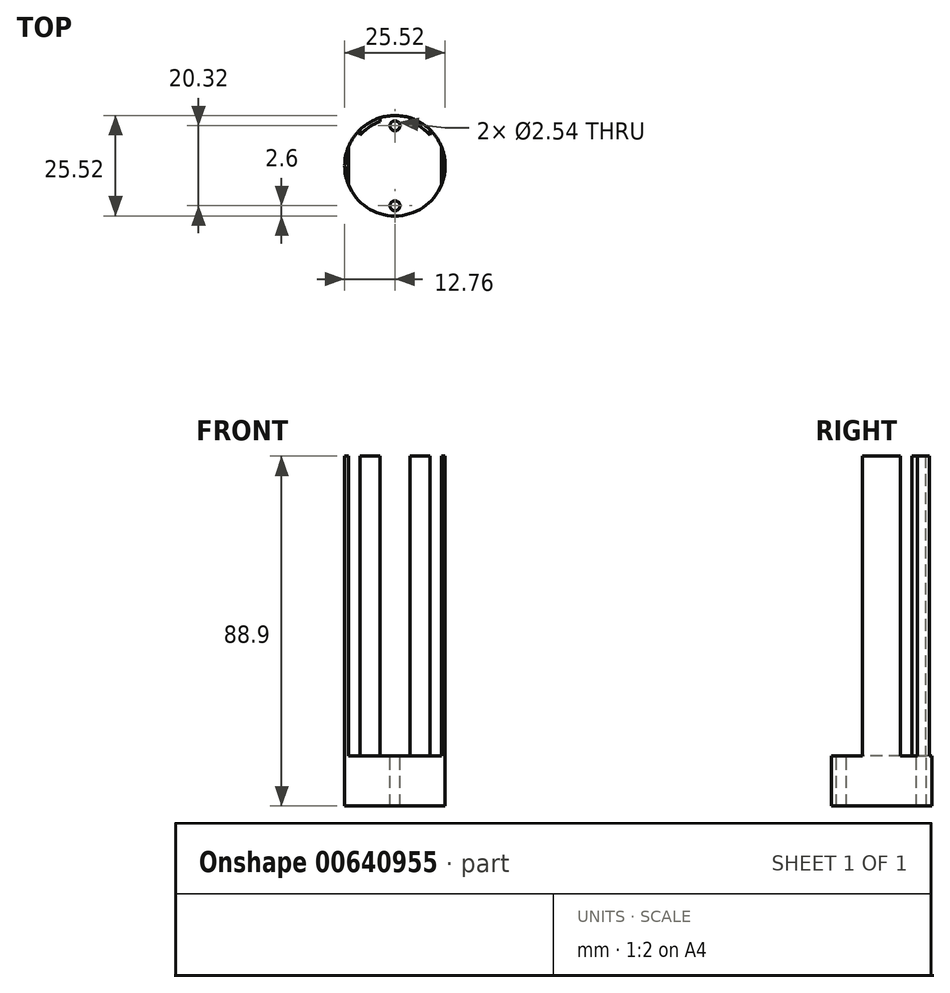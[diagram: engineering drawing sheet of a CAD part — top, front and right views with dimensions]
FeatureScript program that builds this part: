
annotation { "Feature Type Name" : "Feature", "Feature Type Description" : "" }
export const myFeature = defineFeature(function(context is Context, id is Id, definition is map)
    precondition{}
    {
        {
            var Q0;
            Q0=qCreatedBy(makeId("Top.planeOp"),FACE);
            var sketch = newSketch(context, id + "F0", { "sketchPlane" : qUnion([Q0])});
            skArc(sketch, "E0", {"start": v(-3.81, 12.18) * mm, "mid": v(-6.53, 10.97) * mm, "end": v(-8.9, 9.16) * mm});
            skArc(sketch, "E1", {"start": v(-3.81, 11.18) * mm, "mid": v(-6.57, 9.81) * mm, "end": v(-8.9, 7.78) * mm});
            skLineSegment(sketch, "E2", {"start": v(-11.81, 4.84) * mm, "end": v(-11.81, -4.84) * mm});
            skLineSegment(sketch, "E3", {"start": v(11.81, 4.84) * mm, "end": v(11.81, -4.84) * mm});
            skLineSegment(sketch, "E4", {"start": v(-3.81, 12.18) * mm, "end": v(-3.81, 11.18) * mm});
            skLineSegment(sketch, "E5", {"start": v(3.81, 12.18) * mm, "end": v(3.81, 11.18) * mm});
            skLineSegment(sketch, "E6", {"start": v(-8.9, 9.16) * mm, "end": v(-8.9, 7.78) * mm});
            skLineSegment(sketch, "E7", {"start": v(8.9, 9.16) * mm, "end": v(8.9, 7.78) * mm});
            skArc(sketch, "E8.trimOffspring", {"start": v(-11.81, 4.84) * mm, "mid": v(-12.76, 0) * mm, "end": v(-11.81, -4.84) * mm});
            skArc(sketch, "E9.trimOffspring", {"start": v(8.9, 9.16) * mm, "mid": v(6.53, 10.97) * mm, "end": v(3.81, 12.18) * mm});
            skArc(sketch, "E10.trimOffspring", {"start": v(8.9, 7.78) * mm, "mid": v(6.57, 9.81) * mm, "end": v(3.81, 11.18) * mm});
            skArc(sketch, "E11.trimOffspring", {"start": v(11.81, -4.84) * mm, "mid": v(12.76, 0) * mm, "end": v(11.81, 4.84) * mm});
            skSolve(sketch);
        }
        {
            var Q0;
            Q0=qCreatedBy(makeId("Top.planeOp"),FACE);
            var sketch = newSketch(context, id + "F1", { "sketchPlane" : qUnion([Q0])});
            skCircle(sketch, "E12", {"center": v(0, 0) * mm, "radius": 12.76 * mm});
            skPoint(sketch, "E13", {"position": v(0, 10.16) * mm});
            skPoint(sketch, "E14", {"position": v(0, -10.16) * mm});
            skCircle(sketch, "E15", {"center": v(0, 10.16) * mm, "radius": 1.27 * mm});
            skCircle(sketch, "E16", {"center": v(0, -10.16) * mm, "radius": 1.27 * mm});
            skSolve(sketch);
        }
        {
            var Q0;
            Q0 = qSketchRegion(id + "F1", true);
            extrude(context, id + "F2", {"entities" : qUnion([Q0]), "oppositeDirection" : true, "depth" : 12.7 * mm, "offsetDistance" : 25.4 * mm});
        }
        {
            var Q0;
            Q0 = qSketchRegion(id + "F0", true);
            extrude(context, id + "F3", {"entities" : qUnion([Q0]), "operationType" : NewBodyOperationType.ADD, "depth" : 76.2 * mm, "offsetDistance" : 25.4 * mm});
        }
    });
